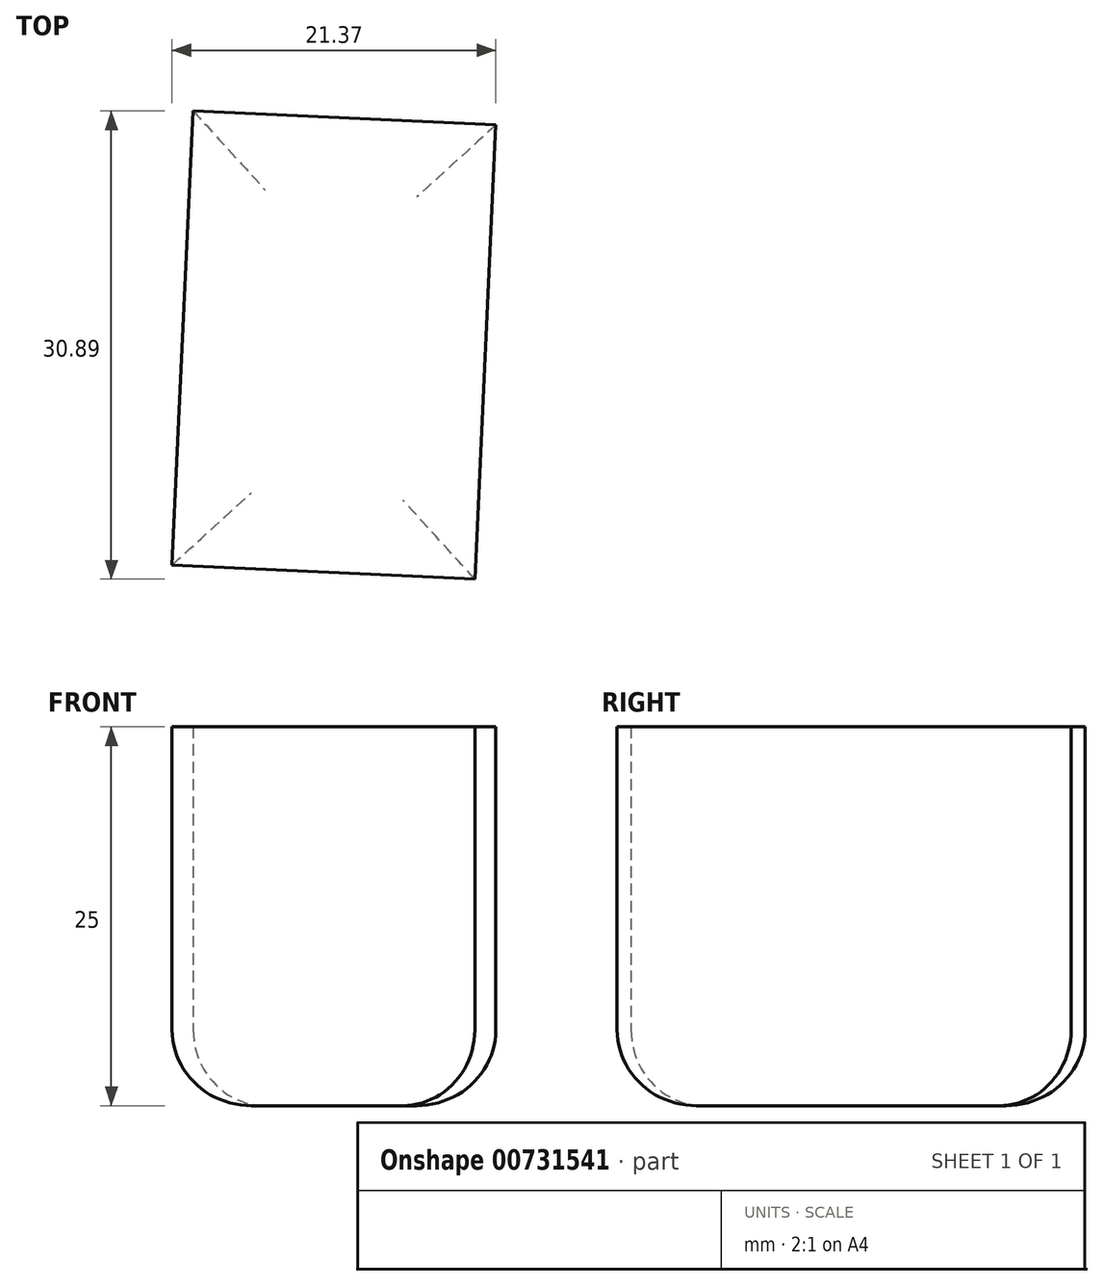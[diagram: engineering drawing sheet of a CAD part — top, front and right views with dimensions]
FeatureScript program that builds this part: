
annotation { "Feature Type Name" : "Feature", "Feature Type Description" : "" }
export const myFeature = defineFeature(function(context is Context, id is Id, definition is map)
    precondition{}
    {
        {
            var Q0;
            Q0=qCreatedBy(makeId("Top.planeOp"),FACE);
            var sketch = newSketch(context, id + "F0", { "sketchPlane" : qUnion([Q0])});
            skLineSegment(sketch, "E0.bottom", {"start": v(-24.76, 51.59) * mm, "end": v(-26.15, 21.62) * mm});
            skLineSegment(sketch, "E0.top", {"start": v(-44.74, 52.51) * mm, "end": v(-46.13, 22.55) * mm});
            skLineSegment(sketch, "E0.left", {"start": v(-24.76, 51.59) * mm, "end": v(-44.74, 52.51) * mm});
            skLineSegment(sketch, "E0.right", {"start": v(-26.15, 21.62) * mm, "end": v(-46.13, 22.55) * mm});
            skLineSegment(sketch, "E1.bottom", {"start": v(-43.87, 52.46) * mm, "end": v(-63.82, 53.96) * mm});
            skLineSegment(sketch, "E1.top", {"start": v(-46.13, 22.55) * mm, "end": v(-66.07, 24.05) * mm});
            skLineSegment(sketch, "E1.left", {"start": v(-46.13, 22.55) * mm, "end": v(-43.87, 52.46) * mm});
            skLineSegment(sketch, "E1.right", {"start": v(-66.07, 24.05) * mm, "end": v(-63.82, 53.96) * mm});
            skSolve(sketch);
        }
        {
            var Q0;
            Q0=makeQuery(id+"F0.imprint","IMPRINT",FACE,{"disambiguationData":[TD([[makeQuery(id+"F0.imprint","IMPRINT",EDGE,{"derivedFrom":sQuery(id+"F0.wireOp",EDGE,"E1.bottom")}),1.0]])]});
            var Q1;
            Q1=makeQuery(id+"F0.imprint","IMPRINT",FACE,{"disambiguationData":[TD([[makeQuery(id+"F0.imprint","IMPRINT",EDGE,{"derivedFrom":sQuery(id+"F0.wireOp",EDGE,"E0.bottom")}),-1.0]])]});
            extrude(context, id + "F1", {"entities" : qUnion([Q0, Q1]), "depth" : 25 * mm, "offsetDistance" : 25 * mm});
        }
        {
            var Q0;
            Q0=makeQuery(id+"F1.opExtrude","CAP_EDGE",EDGE,{"disambiguationData":[OSD([sQuery(id+"F0.wireOp",EDGE,"E1.left")])],"isStart":true});
            var Q1;
            Q1=makeQuery(id+"F1.opExtrude","CAP_EDGE",EDGE,{"disambiguationData":[OSD([sQuery(id+"F0.wireOp",EDGE,"E1.top")])],"isStart":true});
            var Q2;
            Q2=makeQuery(id+"F1.opExtrude","CAP_EDGE",EDGE,{"disambiguationData":[OSD([sQuery(id+"F0.wireOp",EDGE,"E1.right")])],"isStart":true});
            var Q3;
            Q3=makeQuery(id+"F1.opExtrude","CAP_EDGE",EDGE,{"disambiguationData":[OSD([sQuery(id+"F0.wireOp",EDGE,"E1.bottom")])],"isStart":true});
            var Q4;
            Q4=makeQuery(id+"F1.opExtrude","CAP_EDGE",EDGE,{"disambiguationData":[OSD([sQuery(id+"F0.wireOp",EDGE,"E0.top")])],"isStart":true});
            var Q5;
            Q5=makeQuery(id+"F1.opExtrude","CAP_EDGE",EDGE,{"disambiguationData":[OSD([sQuery(id+"F0.wireOp",EDGE,"E0.bottom")])],"isStart":true});
            var Q6;
            Q6=makeQuery(id+"F1.opExtrude","CAP_EDGE",EDGE,{"disambiguationData":[OSD([sQuery(id+"F0.wireOp",EDGE,"E0.right")])],"isStart":true});
            var Q7;
            Q7=makeQuery(id+"F1.opExtrude","CAP_EDGE",EDGE,{"disambiguationData":[OSD([sQuery(id+"F0.wireOp",EDGE,"E0.left")])],"isStart":true});
            fillet(context, id + "F2", {"entities" : qUnion([Q0, Q1, Q2, Q3, Q4, Q5, Q6, Q7]), "radius" : 5 * mm, "tangentPropagation" : true, "allowEdgeOverflow" : false});
        }
    });
